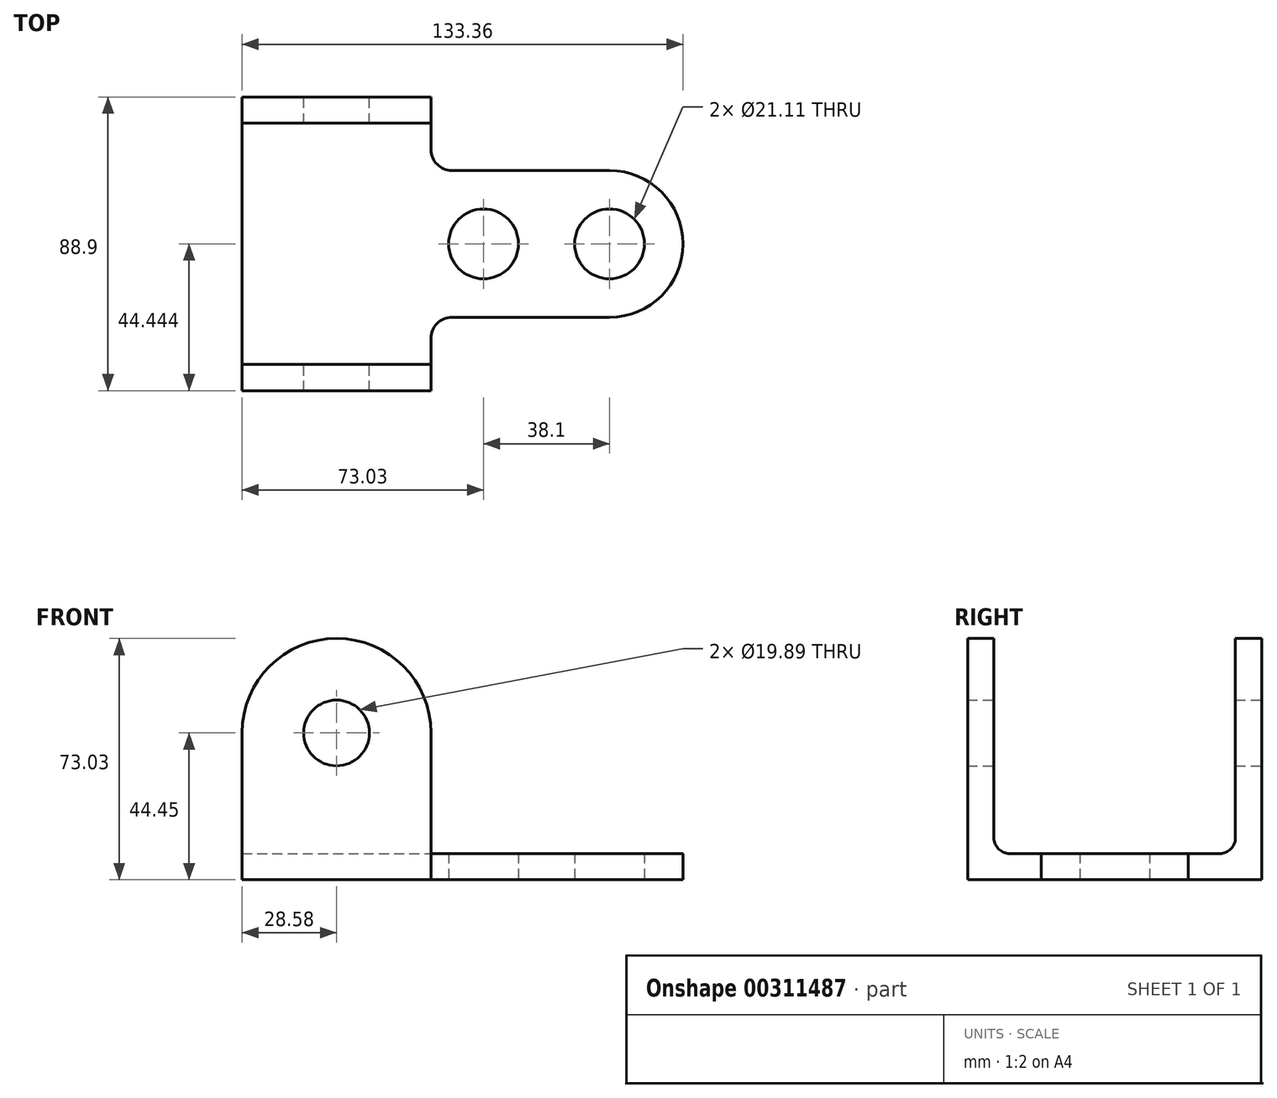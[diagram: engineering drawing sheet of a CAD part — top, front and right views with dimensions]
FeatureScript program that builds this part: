
annotation { "Feature Type Name" : "Feature", "Feature Type Description" : "" }
export const myFeature = defineFeature(function(context is Context, id is Id, definition is map)
    precondition{}
    {
        {
            var Q0;
            Q0=qCreatedBy(makeId("Front.planeOp"),FACE);
            var sketch = newSketch(context, id + "F0", { "sketchPlane" : qUnion([Q0])});
            skArc(sketch, "E0", {"start": v(28.58, 44.45) * mm, "mid": v(0, 73.03) * mm, "end": v(-28.58, 44.45) * mm});
            skLineSegment(sketch, "E1", {"start": v(-28.58, 44.45) * mm, "end": v(-28.57, 0) * mm});
            skLineSegment(sketch, "E2", {"start": v(-28.57, 0) * mm, "end": v(28.57, 0) * mm});
            skLineSegment(sketch, "E3", {"start": v(28.58, 0) * mm, "end": v(28.57, 44.45) * mm});
            skCircle(sketch, "E4", {"center": v(0, 44.45) * mm, "radius": 9.95 * mm});
            skSolve(sketch);
        }
        {
            var Q0;
            Q0 = qSketchRegion(id + "F0", true);
            extrude(context, id + "F1", {"entities" : qUnion([Q0]), "depth" : 88.9 * mm});
        }
        {
            var Q0;
            Q0=makeQuery(id+"F1.opExtrude","SWEPT_FACE",FACE,{"disambiguationData":[OSD([sQuery(id+"F0.wireOp",EDGE,"E3")])]});
            var sketch = newSketch(context, id + "F2", { "sketchPlane" : qUnion([Q0])});
            skLineSegment(sketch, "E5", {"start": v(-80.96, 77.54) * mm, "end": v(-80.96, 12.7) * mm});
            skLineSegment(sketch, "E6", {"start": v(-76.2, 7.94) * mm, "end": v(-12.71, 7.94) * mm});
            skLineSegment(sketch, "E7", {"start": v(-7.94, 12.71) * mm, "end": v(-7.94, 77.54) * mm});
            skLineSegment(sketch, "E8", {"start": v(-7.94, 77.54) * mm, "end": v(-80.96, 77.54) * mm});
            skArc(sketch, "E9", {"start": v(-80.96, 12.7) * mm, "mid": v(-79.57, 9.33) * mm, "end": v(-76.2, 7.94) * mm});
            skArc(sketch, "E10", {"start": v(-12.71, 7.94) * mm, "mid": v(-9.34, 9.34) * mm, "end": v(-7.94, 12.71) * mm});
            skSolve(sketch);
        }
        {
            var Q0;
            Q0 = qSketchRegion(id + "F2", true);
            extrude(context, id + "F3", {"entities" : qUnion([Q0]), "operationType" : NewBodyOperationType.REMOVE, "endBound" : BoundingType.THROUGH_ALL, "oppositeDirection" : true, "depth" : 25.4 * mm});
        }
        {
            var Q0;
            Q0=qCreatedBy(makeId("Top.planeOp"),FACE);
            var sketch = newSketch(context, id + "F4", { "sketchPlane" : qUnion([Q0])});
            skArc(sketch, "E11", {"start": v(28.58, -15.88) * mm, "mid": v(30.43, -20.37) * mm, "end": v(34.93, -22.23) * mm});
            skArc(sketch, "E12", {"start": v(34.93, -66.68) * mm, "mid": v(30.43, -68.54) * mm, "end": v(28.58, -73.03) * mm});
            skLineSegment(sketch, "E13", {"start": v(34.93, -22.23) * mm, "end": v(82.55, -22.23) * mm});
            skLineSegment(sketch, "E14", {"start": v(34.93, -66.68) * mm, "end": v(82.55, -66.68) * mm});
            skArc(sketch, "E15", {"start": v(82.55, -66.68) * mm, "mid": v(104.78, -44.46) * mm, "end": v(82.55, -22.23) * mm});
            skLineSegment(sketch, "E16", {"start": v(28.57, -12.71) * mm, "end": v(28.58, -76.2) * mm, "construction": true});
            skPoint(sketch, "E17", {"position": v(28.58, -44.46) * mm});
            skLineSegment(sketch, "E18", {"start": v(28.58, -15.88) * mm, "end": v(28.58, -73.03) * mm, "construction": true});
            skLineSegment(sketch, "E19", {"start": v(28.58, -44.46) * mm, "end": v(116.1, -44.46) * mm, "construction": true});
            skPoint(sketch, "E19.endSnap0", {"position": v(104.78, -44.46) * mm});
            skCircle(sketch, "E20", {"center": v(44.45, -44.46) * mm, "radius": 10.55 * mm});
            skCircle(sketch, "E21", {"center": v(82.55, -44.46) * mm, "radius": 10.55 * mm});
            skLineSegment(sketch, "E22", {"start": v(28.58, -15.88) * mm, "end": v(28.58, -73.03) * mm});
            skSolve(sketch);
        }
        {
            var Q0;
            Q0 = qSketchRegion(id + "F4", true);
            extrude(context, id + "F5", {"entities" : qUnion([Q0]), "operationType" : NewBodyOperationType.ADD, "depth" : 7.94 * mm});
        }
    });
